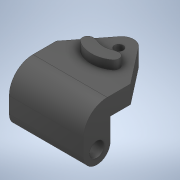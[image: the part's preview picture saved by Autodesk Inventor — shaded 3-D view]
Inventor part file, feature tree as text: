
AUTODESK INVENTOR PART (.ipt)
format: ipt  version: 2020 (Build 240168000, 168)  size: 223,232 bytes
history: native  units: in
note: dims shown in document units (in); Inventor stores cm internally (conversion verified against a paired STEP export)
features: extrude x2, sketch x2, projected_geometry x1
ambient origin geometry x8: Origin, YZ Plane, XZ Plane, XY Plane, X Axis, Y Axis, Z Axis, Center Point
bodies: Solid2 (feature_tree), Solid1 (feature_tree)
feature tree (5):
  extrude  "make bean smaller"  Depth=0.3937in TaperAngle=0.0deg
  extrude  "make bottom plate space bigger"  Depth=0.126in TaperAngle=0.0deg
  sketch  "Sketch2"  dims[d7=0.0039in d8=0.3937in d9=0.0in]
  projected_geometry  "Projected Loop1"
  sketch  "Sketch4"  dims[d13=0.0118in d14=0.126in d15=0.0in]
